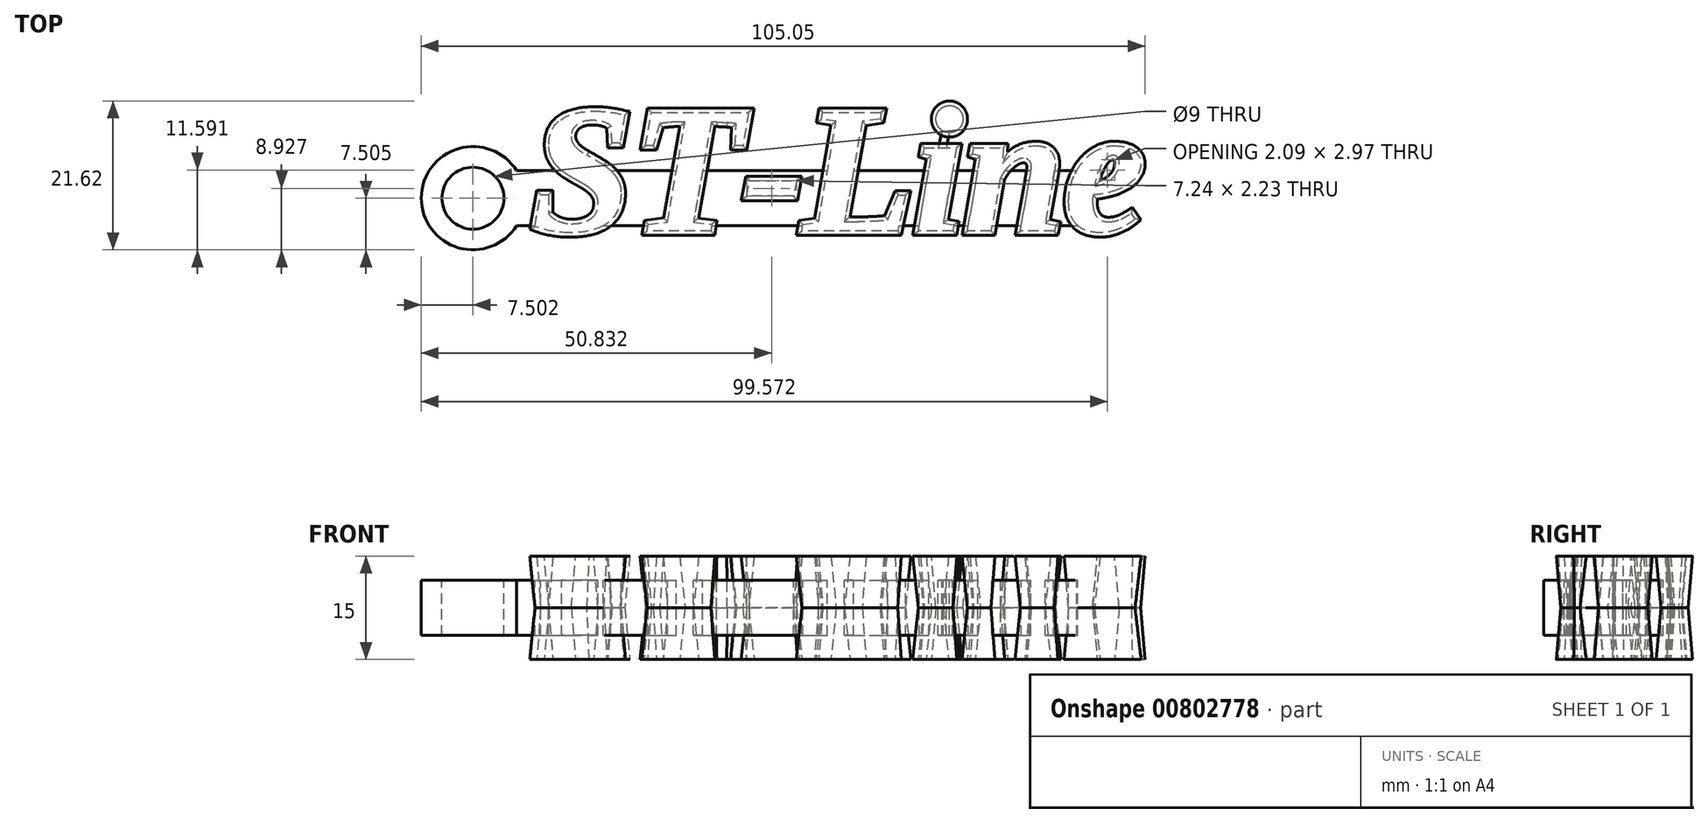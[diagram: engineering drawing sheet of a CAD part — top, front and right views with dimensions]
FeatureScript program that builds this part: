
annotation { "Feature Type Name" : "Feature", "Feature Type Description" : "" }
export const myFeature = defineFeature(function(context is Context, id is Id, definition is map)
    precondition{}
    {
        {
            var Q0;
            Q0=qCreatedBy(makeId("Top.planeOp"),FACE);
            var sketch = newSketch(context, id + "F0", { "sketchPlane" : qUnion([Q0])});
            skLineSegment(sketch, "E0.bottom", {"start": v(-28.43, -20.25) * mm, "end": v(61.57, -20.25) * mm});
            skLineSegment(sketch, "E0.top", {"start": v(-28.43, -28.25) * mm, "end": v(61.57, -28.25) * mm});
            skLineSegment(sketch, "E0.left", {"start": v(-28.43, -20.25) * mm, "end": v(-28.43, -28.25) * mm});
            skLineSegment(sketch, "E0.right", {"start": v(61.57, -20.25) * mm, "end": v(61.57, -28.25) * mm});
            skCircle(sketch, "E1", {"center": v(-28.43, -24.25) * mm, "radius": 7.5 * mm});
            skCircle(sketch, "E2.0", {"center": v(-28.43, -24.25) * mm, "radius": 4.5 * mm});
            skText(sketch, "E3", { "text": "ST-Line", "fontName": "Tinos-BoldItalic.ttf"});
            skLineSegment(sketch, "E4", {"start": v(39.78, -13.79) * mm, "end": v(38.95, -17.57) * mm});
            skLineSegment(sketch, "E5.0", {"start": v(40.88, -14.03) * mm, "end": v(40.04, -17.8) * mm});
            const initialGuessF0  = {"E3": [-0.0199, -0.029, 1, 0, 0.0189]};
            skSetInitialGuess(sketch, initialGuessF0);
            skSolve(sketch);
        }
        {
            var Q0;
            {var subQ0=sQuery(id+"F0.wireOp",EDGE,"E1");var subQ1=sQuery(id+"F0.wireOp",EDGE,"E0.bottom");var subQ2=makeQuery(id+"F0.imprint","INTERSECT",VERTEX,{"derivedFrom":[subQ1,subQ0]});Q0=makeQuery(id+"F0.imprint","IMPRINT",FACE,{"disambiguationData":[TD([[makeQuery(id+"F0.imprint","IMPRINT",EDGE,{"disambiguationData":[TD([[subQ2,1.0]])],"derivedFrom":subQ1}),-1.0]])]});}
            var Q1;
            {var subQ0=sQuery(id+"F0.wireOp",EDGE,"E1");var subQ1=sQuery(id+"F0.wireOp",EDGE,"E0.bottom");var subQ2=makeQuery(id+"F0.imprint","INTERSECT",VERTEX,{"derivedFrom":[subQ1,subQ0]});Q1=makeQuery(id+"F0.imprint","IMPRINT",FACE,{"disambiguationData":[TD([[makeQuery(id+"F0.imprint","IMPRINT",EDGE,{"disambiguationData":[TD([[subQ2,1.0]])],"derivedFrom":subQ1}),1.0]])]});}
            var Q2;
            {var subQ0=sQuery(id+"F0.wireOp",EDGE,"E3.sketch_text.stroke-2");Q2=makeQuery(id+"F0.imprint","IMPRINT",FACE,{"disambiguationData":[TD([[makeQuery(id+"F0.imprint","IMPRINT",EDGE,{"derivedFrom":subQ0}),1.0]])]});}
            var Q3;
            {var subQ0=sQuery(id+"F0.wireOp",EDGE,"E3.sketch_text.stroke-29");Q3=makeQuery(id+"F0.imprint","IMPRINT",FACE,{"disambiguationData":[TD([[makeQuery(id+"F0.imprint","IMPRINT",EDGE,{"derivedFrom":subQ0}),1.0]])]});}
            var Q4;
            {var subQ6=sQuery(id+"F0.wireOp",EDGE,"E3.sketch_text.stroke-50");Q4=makeQuery(id+"F0.imprint","IMPRINT",FACE,{"disambiguationData":[TD([[makeQuery(id+"F0.imprint","IMPRINT",EDGE,{"derivedFrom":subQ6}),1.0]])]});}
            var Q5;
            {var subQ0=sQuery(id+"F0.wireOp",EDGE,"E3.sketch_text.stroke-57");Q5=makeQuery(id+"F0.imprint","IMPRINT",FACE,{"disambiguationData":[TD([[makeQuery(id+"F0.imprint","IMPRINT",EDGE,{"derivedFrom":subQ0}),1.0]])]});}
            var Q6;
            {var subQ1=sQuery(id+"F0.wireOp",EDGE,"E3.sketch_text.stroke-73");Q6=makeQuery(id+"F0.imprint","IMPRINT",FACE,{"disambiguationData":[TD([[makeQuery(id+"F0.imprint","IMPRINT",EDGE,{"derivedFrom":subQ1}),1.0]])]});}
            var Q7;
            {var subQ1=sQuery(id+"F0.wireOp",EDGE,"E3.sketch_text.stroke-91");var subQ9=sQuery(id+"F0.wireOp",EDGE,"E0.bottom");var subQ11=makeQuery(id+"F0.imprint","INTERSECT",VERTEX,{"derivedFrom":[subQ9,subQ1]});Q7=makeQuery(id+"F0.imprint","IMPRINT",FACE,{"disambiguationData":[TD([[makeQuery(id+"F0.imprint","IMPRINT",EDGE,{"disambiguationData":[TD([[subQ11,-1.0]])],"derivedFrom":subQ9}),-1.0]])]});}
            var Q8;
            {var subQ0=sQuery(id+"F0.wireOp",EDGE,"E3.sketch_text.stroke-103");Q8=makeQuery(id+"F0.imprint","IMPRINT",FACE,{"disambiguationData":[TD([[makeQuery(id+"F0.imprint","IMPRINT",EDGE,{"derivedFrom":subQ0}),1.0]])]});}
            var Q9;
            {var subQ0=sQuery(id+"F0.wireOp",EDGE,"E4");var subQ1=sQuery(id+"F0.wireOp",EDGE,"E3.sketch_text.stroke-79");var subQ2=makeQuery(id+"F0.imprint","INTERSECT",VERTEX,{"derivedFrom":[subQ1,subQ0]});Q9=makeQuery(id+"F0.imprint","IMPRINT",FACE,{"disambiguationData":[TD([[makeQuery(id+"F0.imprint","IMPRINT",EDGE,{"disambiguationData":[TD([[subQ2,-1.0]])],"derivedFrom":subQ1}),1.0]])]});}
            extrude(context, id + "F1", {"entities" : qUnion([Q0, Q1, Q2, Q3, Q4, Q5, Q6, Q7, Q8, Q9]), "endBound" : BoundingType.SYMMETRIC, "oppositeDirection" : true, "depth" : 8 * mm, "offsetDistance" : 25 * mm});
        }
        {
            var Q0;
            {var subQ5=sQuery(id+"F0.wireOp",EDGE,"E3.sketch_text.stroke-14");Q0=makeQuery(id+"F0.imprint","IMPRINT",FACE,{"disambiguationData":[TD([[makeQuery(id+"F0.imprint","IMPRINT",EDGE,{"derivedFrom":subQ5}),-1.0]])]});}
            var Q1;
            {var subQ6=sQuery(id+"F0.wireOp",EDGE,"E3.sketch_text.stroke-2");Q1=makeQuery(id+"F0.imprint","IMPRINT",FACE,{"disambiguationData":[TD([[makeQuery(id+"F0.imprint","IMPRINT",EDGE,{"derivedFrom":subQ6}),-1.0]])]});}
            var Q2;
            {var subQ0=sQuery(id+"F0.wireOp",EDGE,"E3.sketch_text.stroke-36");Q2=makeQuery(id+"F0.imprint","IMPRINT",FACE,{"disambiguationData":[TD([[makeQuery(id+"F0.imprint","IMPRINT",EDGE,{"derivedFrom":subQ0}),-1.0]])]});}
            var Q3;
            {var subQ0=sQuery(id+"F0.wireOp",EDGE,"E3.sketch_text.stroke-34");Q3=makeQuery(id+"F0.imprint","IMPRINT",FACE,{"disambiguationData":[TD([[makeQuery(id+"F0.imprint","IMPRINT",EDGE,{"derivedFrom":subQ0}),-1.0]])]});}
            var Q4;
            {var subQ0=sQuery(id+"F0.wireOp",EDGE,"E3.sketch_text.stroke-67");Q4=makeQuery(id+"F0.imprint","IMPRINT",FACE,{"disambiguationData":[TD([[makeQuery(id+"F0.imprint","IMPRINT",EDGE,{"derivedFrom":subQ0}),-1.0]])]});}
            var Q5;
            {var subQ7=sQuery(id+"F0.wireOp",EDGE,"E3.sketch_text.stroke-57");Q5=makeQuery(id+"F0.imprint","IMPRINT",FACE,{"disambiguationData":[TD([[makeQuery(id+"F0.imprint","IMPRINT",EDGE,{"derivedFrom":subQ7}),-1.0]])]});}
            var Q6;
            Q6=makeQuery(id+"F0.imprint","IMPRINT",FACE,{"disambiguationData":[TD([[makeQuery(id+"F0.imprint","IMPRINT",EDGE,{"derivedFrom":sQuery(id+"F0.wireOp",EDGE,"E3.sketch_text.stroke-53")}),-1.0]])]});
            var Q7;
            {var subQ1=sQuery(id+"F0.wireOp",EDGE,"E3.sketch_text.stroke-73");Q7=makeQuery(id+"F0.imprint","IMPRINT",FACE,{"disambiguationData":[TD([[makeQuery(id+"F0.imprint","IMPRINT",EDGE,{"derivedFrom":subQ1}),-1.0]])]});}
            var Q8;
            {var subQ0=sQuery(id+"F0.wireOp",EDGE,"E3.sketch_text.stroke-77");Q8=makeQuery(id+"F0.imprint","IMPRINT",FACE,{"disambiguationData":[TD([[makeQuery(id+"F0.imprint","IMPRINT",EDGE,{"derivedFrom":subQ0}),-1.0]])]});}
            var Q9;
            Q9=makeQuery(id+"F0.imprint","IMPRINT",FACE,{"disambiguationData":[TD([[makeQuery(id+"F0.imprint","IMPRINT",EDGE,{"derivedFrom":sQuery(id+"F0.wireOp",EDGE,"E3.sketch_text.stroke-81")}),-1.0]])]});
            var Q10;
            {var subQ8=sQuery(id+"F0.wireOp",EDGE,"E3.sketch_text.stroke-89");Q10=makeQuery(id+"F0.imprint","IMPRINT",FACE,{"disambiguationData":[TD([[makeQuery(id+"F0.imprint","IMPRINT",EDGE,{"derivedFrom":subQ8}),-1.0]])]});}
            var Q11;
            {var subQ5=sQuery(id+"F0.wireOp",EDGE,"E0.bottom");var subQ7=sQuery(id+"F0.wireOp",EDGE,"E3.sketch_text.stroke-94");var subQ9=makeQuery(id+"F0.imprint","INTERSECT",VERTEX,{"derivedFrom":[subQ5,subQ7]});Q11=makeQuery(id+"F0.imprint","IMPRINT",FACE,{"disambiguationData":[TD([[makeQuery(id+"F0.imprint","IMPRINT",EDGE,{"disambiguationData":[TD([[subQ9,-1.0]])],"derivedFrom":subQ5}),-1.0]])]});}
            var Q12;
            {var subQ0=sQuery(id+"F0.wireOp",EDGE,"E3.sketch_text.stroke-103");Q12=makeQuery(id+"F0.imprint","IMPRINT",FACE,{"disambiguationData":[TD([[makeQuery(id+"F0.imprint","IMPRINT",EDGE,{"derivedFrom":subQ0}),-1.0]])]});}
            var Q13;
            {var subQ5=sQuery(id+"F0.wireOp",EDGE,"E3.sketch_text.stroke-0");Q13=makeQuery(id+"F0.imprint","IMPRINT",FACE,{"disambiguationData":[TD([[makeQuery(id+"F0.imprint","IMPRINT",EDGE,{"derivedFrom":subQ5}),-1.0]])]});}
            var Q14;
            {var subQ5=sQuery(id+"F0.wireOp",EDGE,"E3.sketch_text.stroke-52");Q14=makeQuery(id+"F0.imprint","IMPRINT",FACE,{"disambiguationData":[TD([[makeQuery(id+"F0.imprint","IMPRINT",EDGE,{"derivedFrom":subQ5}),-1.0]])]});}
            var Q15;
            {var subQ5=sQuery(id+"F0.wireOp",EDGE,"E3.sketch_text.stroke-63");Q15=makeQuery(id+"F0.imprint","IMPRINT",FACE,{"disambiguationData":[TD([[makeQuery(id+"F0.imprint","IMPRINT",EDGE,{"derivedFrom":subQ5}),-1.0]])]});}
            var Q16;
            {var subQ5=sQuery(id+"F0.wireOp",EDGE,"E3.sketch_text.stroke-75");Q16=makeQuery(id+"F0.imprint","IMPRINT",FACE,{"disambiguationData":[TD([[makeQuery(id+"F0.imprint","IMPRINT",EDGE,{"derivedFrom":subQ5}),-1.0]])]});}
            var Q17;
            {var subQ5=sQuery(id+"F0.wireOp",EDGE,"E3.sketch_text.stroke-93");Q17=makeQuery(id+"F0.imprint","IMPRINT",FACE,{"disambiguationData":[TD([[makeQuery(id+"F0.imprint","IMPRINT",EDGE,{"derivedFrom":subQ5}),-1.0]])]});}
            var Q18;
            {var subQ5=sQuery(id+"F0.wireOp",EDGE,"E3.sketch_text.stroke-106");Q18=makeQuery(id+"F0.imprint","IMPRINT",FACE,{"disambiguationData":[TD([[makeQuery(id+"F0.imprint","IMPRINT",EDGE,{"derivedFrom":subQ5}),-1.0]])]});}
            var Q19;
            {var subQ5=sQuery(id+"F0.wireOp",EDGE,"E3.sketch_text.stroke-112");Q19=makeQuery(id+"F0.imprint","IMPRINT",FACE,{"disambiguationData":[TD([[makeQuery(id+"F0.imprint","IMPRINT",EDGE,{"derivedFrom":subQ5}),-1.0]])]});}
            var Q20;
            {var subQ0=sQuery(id+"F0.wireOp",EDGE,"E3.sketch_text.stroke-114");Q20=makeQuery(id+"F0.imprint","IMPRINT",FACE,{"disambiguationData":[TD([[makeQuery(id+"F0.imprint","IMPRINT",EDGE,{"derivedFrom":subQ0}),-1.0]])]});}
            var Q21;
            Q21=makeQuery(id+"F0.imprint","IMPRINT",FACE,{"disambiguationData":[TD([[makeQuery(id+"F0.imprint","IMPRINT",EDGE,{"derivedFrom":sQuery(id+"F0.wireOp",EDGE,"E3.sketch_text.stroke-109")}),-1.0]])]});
            extrude(context, id + "F2", {"entities" : qUnion([Q0, Q1, Q2, Q3, Q4, Q5, Q6, Q7, Q8, Q9, Q10, Q11, Q12, Q13, Q14, Q15, Q16, Q17, Q18, Q19, Q20, Q21]), "endBound" : BoundingType.SYMMETRIC, "depth" : 15 * mm, "offsetDistance" : 25 * mm, "hasDraft" : true, "draftAngle" : 5 * degree});
        }
    });
